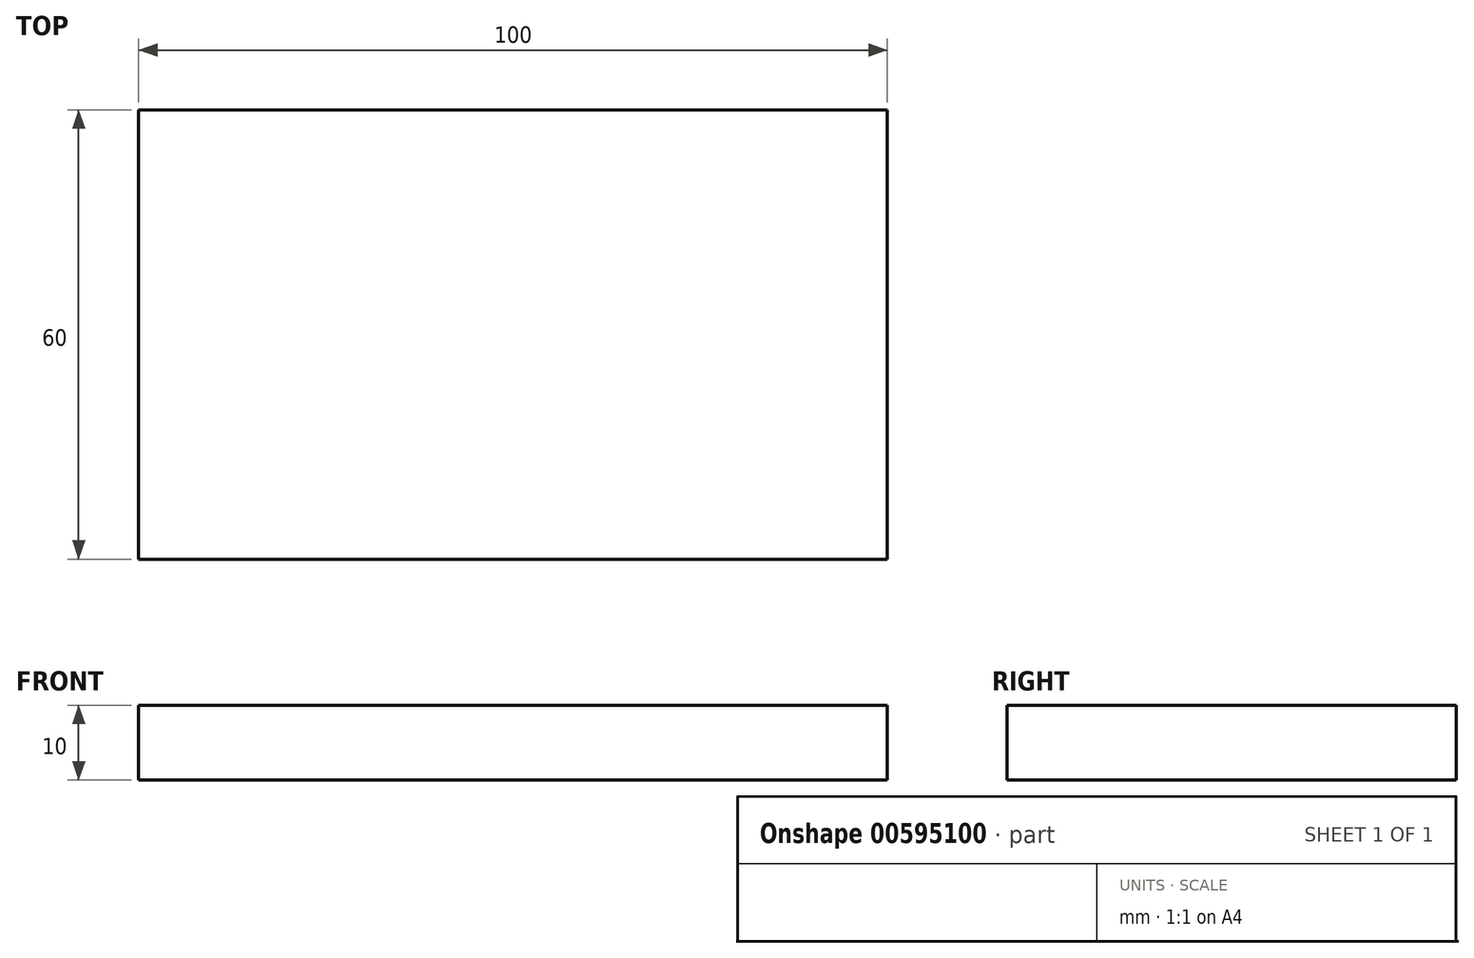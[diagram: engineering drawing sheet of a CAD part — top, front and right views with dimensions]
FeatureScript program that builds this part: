
annotation { "Feature Type Name" : "Feature", "Feature Type Description" : "" }
export const myFeature = defineFeature(function(context is Context, id is Id, definition is map)
    precondition{}
    {
        {
            var Q0;
            Q0=qCreatedBy(makeId("Top.planeOp"),FACE);
            var sketch = newSketch(context, id + "F0", { "sketchPlane" : qUnion([Q0])});
            skLineSegment(sketch, "E0.bottom", {"start": v(-117.72, 0) * mm, "end": v(-17.72, 0) * mm});
            skLineSegment(sketch, "E0.top", {"start": v(-117.72, -60) * mm, "end": v(-17.72, -60) * mm});
            skLineSegment(sketch, "E0.left", {"start": v(-117.72, 0) * mm, "end": v(-117.72, -60) * mm});
            skLineSegment(sketch, "E0.right", {"start": v(-17.72, 0) * mm, "end": v(-17.72, -60) * mm});
            skLineSegment(sketch, "E1", {"start": v(-67.72, -60) * mm, "end": v(-67.72, 0) * mm});
            skSolve(sketch);
        }
        {
            var Q0;
            Q0=qSketchRegion(id+"F0",true);
            extrude(context, id + "F1", {"entities" : qUnion([Q0]), "depth" : 10 * mm, "offsetDistance" : 25.4 * mm});
        }
    });
